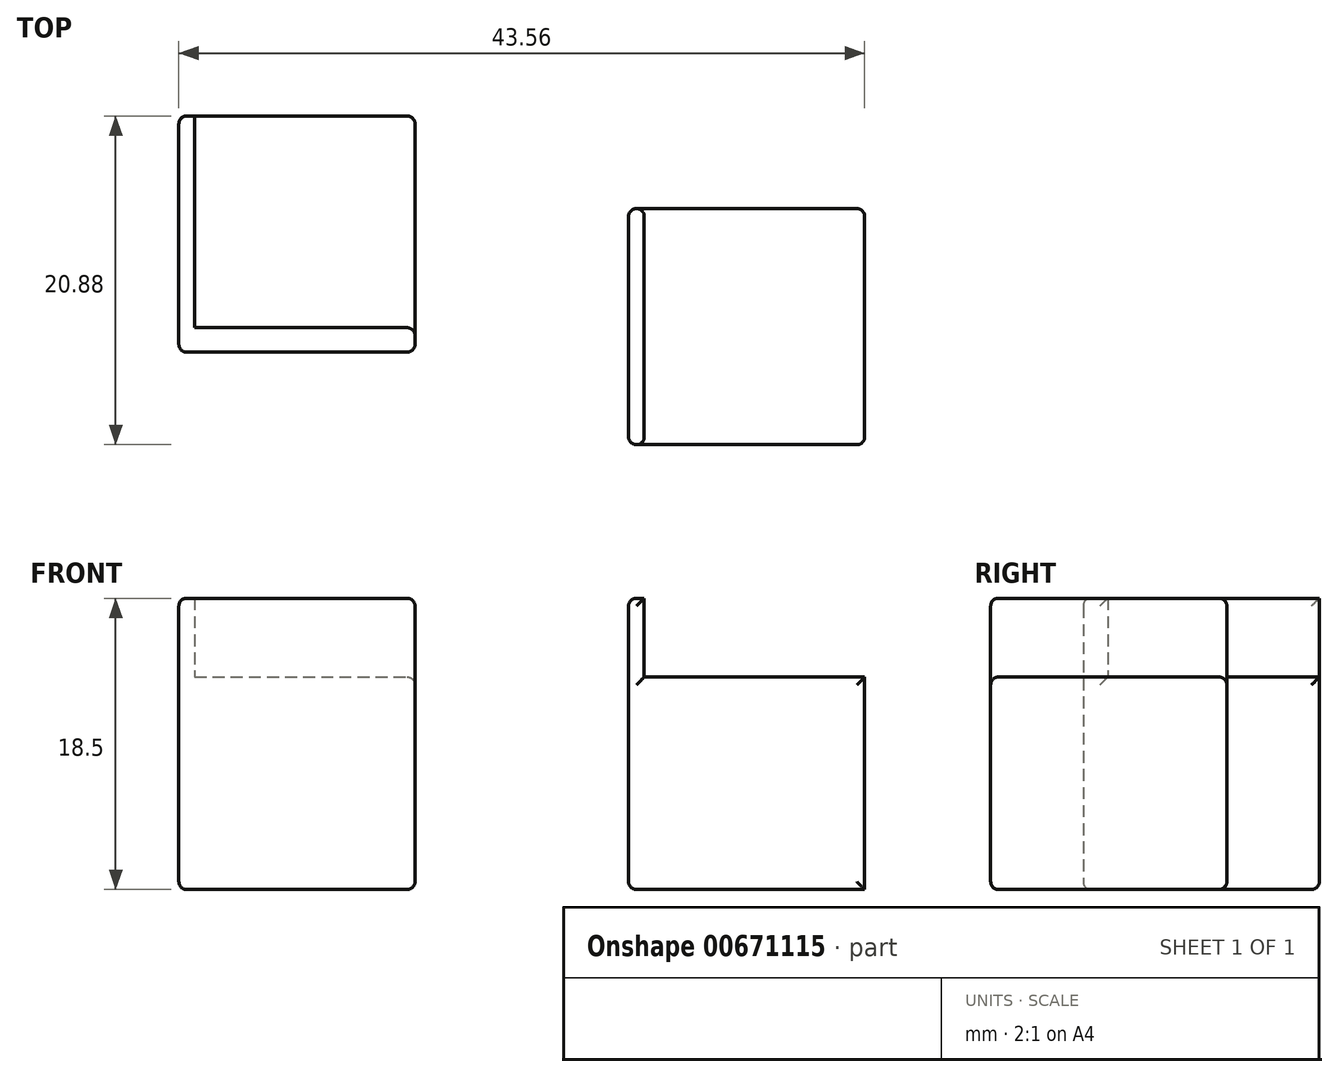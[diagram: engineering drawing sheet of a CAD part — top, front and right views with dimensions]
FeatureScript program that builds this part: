
annotation { "Feature Type Name" : "Feature", "Feature Type Description" : "" }
export const myFeature = defineFeature(function(context is Context, id is Id, definition is map)
    precondition{}
    {
        {
            var Q0;
            Q0=qCreatedBy(makeId("Top.planeOp"),FACE);
            var sketch = newSketch(context, id + "F0", { "sketchPlane" : qUnion([Q0])});
            skLineSegment(sketch, "E0.bottom", {"start": v(-22.19, -22.69) * mm, "end": v(-7.19, -22.69) * mm});
            skLineSegment(sketch, "E0.top", {"start": v(-22.19, -37.69) * mm, "end": v(-7.19, -37.69) * mm});
            skLineSegment(sketch, "E0.left", {"start": v(-22.19, -22.69) * mm, "end": v(-22.19, -37.69) * mm});
            skLineSegment(sketch, "E0.right", {"start": v(-7.19, -22.69) * mm, "end": v(-7.19, -37.69) * mm});
            skSolve(sketch);
        }
        {
            var Q0;
            Q0=makeQuery(id+"F0.imprint","IMPRINT",FACE,{"disambiguationData":[TD([[makeQuery(id+"F0.imprint","IMPRINT",EDGE,{"derivedFrom":sQuery(id+"F0.wireOp",EDGE,"E0.bottom")}),-1.0]])]});
            extrude(context, id + "F1", {"entities" : qUnion([Q0]), "depth" : 13.5 * mm, "offsetDistance" : 25 * mm});
        }
        {
            var Q0;
            Q0=makeQuery(id+"F1.opExtrude","CAP_FACE",FACE,{"disambiguationData":[OSD([sQuery(id+"F0.wireOp",EDGE,"E0.bottom"),sQuery(id+"F0.wireOp",EDGE,"E0.top"),sQuery(id+"F0.wireOp",EDGE,"E0.left"),sQuery(id+"F0.wireOp",EDGE,"E0.right")])],"isStart":false});
            var sketch = newSketch(context, id + "F2", { "sketchPlane" : qUnion([Q0])});
            skLineSegment(sketch, "E1.bottom", {"start": v(-22.19, -22.69) * mm, "end": v(-21.19, -22.69) * mm});
            skLineSegment(sketch, "E1.top", {"start": v(-22.19, -37.69) * mm, "end": v(-21.19, -37.69) * mm});
            skLineSegment(sketch, "E1.left", {"start": v(-22.19, -22.69) * mm, "end": v(-22.19, -37.69) * mm});
            skLineSegment(sketch, "E1.right", {"start": v(-21.19, -22.69) * mm, "end": v(-21.19, -37.69) * mm});
            skLineSegment(sketch, "E2.bottom", {"start": v(-22.19, -37.69) * mm, "end": v(-7.19, -37.69) * mm});
            skLineSegment(sketch, "E2.top", {"start": v(-22.19, -36.13) * mm, "end": v(-7.19, -36.13) * mm});
            skLineSegment(sketch, "E2.left", {"start": v(-22.19, -37.69) * mm, "end": v(-22.19, -36.13) * mm});
            skLineSegment(sketch, "E2.right", {"start": v(-7.19, -37.69) * mm, "end": v(-7.19, -36.13) * mm});
            skSolve(sketch);
        }
        {
            var Q0;
            Q0 = qSketchRegion(id + "F2", true);
            extrude(context, id + "F3", {"entities" : qUnion([Q0]), "operationType" : NewBodyOperationType.ADD, "depth" : 5 * mm, "offsetDistance" : 25 * mm});
        }
        {
            var Q0;
            Q0 = qSketchRegion(id + "F2", true);
            extrude(context, id + "F4", {"entities" : qUnion([Q0]), "operationType" : NewBodyOperationType.ADD, "depth" : 5 * mm, "offsetDistance" : 25 * mm});
        }
        {
            var Q0;
            Q0=makeQuery(id+"F3.boolean.opBoolean","MERGE",FACE,{"derivedFrom":[makeQuery(id+"F1.opExtrude","SWEPT_FACE",FACE,{"disambiguationData":[OSD([sQuery(id+"F0.wireOp",EDGE,"E0.left")])]}),makeQuery(id+"F3.opExtrude","SWEPT_FACE",FACE,{"disambiguationData":[OSD([sQuery(id+"F2.wireOp",EDGE,"E1.left"),sQuery(id+"F2.wireOp",EDGE,"E2.left")])]})]});
            var Q1;
            Q1=makeQuery(id+"F3.boolean.opBoolean","MERGE",FACE,{"derivedFrom":[makeQuery(id+"F1.opExtrude","SWEPT_FACE",FACE,{"disambiguationData":[OSD([sQuery(id+"F0.wireOp",EDGE,"E0.top")])]}),makeQuery(id+"F3.opExtrude","SWEPT_FACE",FACE,{"disambiguationData":[OSD([sQuery(id+"F2.wireOp",EDGE,"E2.bottom")])]})]});
            var Q2;
            Q2=makeQuery(id+"F1.opExtrude","CAP_FACE",FACE,{"disambiguationData":[OSD([sQuery(id+"F0.wireOp",EDGE,"E0.bottom"),sQuery(id+"F0.wireOp",EDGE,"E0.top"),sQuery(id+"F0.wireOp",EDGE,"E0.left"),sQuery(id+"F0.wireOp",EDGE,"E0.right")])],"isStart":true});
            var Q3;
            Q3=makeQuery(id+"F3.boolean.opBoolean","MERGE",FACE,{"derivedFrom":[makeQuery(id+"F1.opExtrude","SWEPT_FACE",FACE,{"disambiguationData":[OSD([sQuery(id+"F0.wireOp",EDGE,"E0.right")])]}),makeQuery(id+"F3.opExtrude","SWEPT_FACE",FACE,{"disambiguationData":[OSD([sQuery(id+"F2.wireOp",EDGE,"E2.right")])]})]});
            fillet(context, id + "F5", {"entities" : qUnion([Q0, Q1, Q2, Q3]), "radius" : 0.5 * mm, "tangentPropagation" : true, "allowEdgeOverflow" : false});
        }
        {
            var Q0;
            Q0=qCreatedBy(makeId("Top.planeOp"),FACE);
            var sketch = newSketch(context, id + "F6", { "sketchPlane" : qUnion([Q0])});
            skLineSegment(sketch, "E3.bottom", {"start": v(6.37, -28.57) * mm, "end": v(21.37, -28.57) * mm});
            skLineSegment(sketch, "E3.top", {"start": v(6.37, -43.57) * mm, "end": v(21.37, -43.57) * mm});
            skLineSegment(sketch, "E3.left", {"start": v(6.37, -28.57) * mm, "end": v(6.37, -43.57) * mm});
            skLineSegment(sketch, "E3.right", {"start": v(21.37, -28.57) * mm, "end": v(21.37, -43.57) * mm});
            skSolve(sketch);
        }
        {
            var Q0;
            Q0 = qSketchRegion(id + "F6", true);
            extrude(context, id + "F7", {"entities" : qUnion([Q0]), "depth" : 13.5 * mm, "offsetDistance" : 25 * mm});
        }
        {
            var Q0;
            Q0=makeQuery(id+"F7.opExtrude","CAP_FACE",FACE,{"disambiguationData":[OSD([sQuery(id+"F6.wireOp",EDGE,"E3.bottom"),sQuery(id+"F6.wireOp",EDGE,"E3.top"),sQuery(id+"F6.wireOp",EDGE,"E3.left"),sQuery(id+"F6.wireOp",EDGE,"E3.right")])],"isStart":false});
            var sketch = newSketch(context, id + "F8", { "sketchPlane" : qUnion([Q0])});
            skLineSegment(sketch, "E4.bottom", {"start": v(6.37, -43.57) * mm, "end": v(7.37, -43.57) * mm});
            skLineSegment(sketch, "E4.top", {"start": v(6.37, -28.57) * mm, "end": v(7.37, -28.57) * mm});
            skLineSegment(sketch, "E4.left", {"start": v(6.37, -43.57) * mm, "end": v(6.37, -28.57) * mm});
            skLineSegment(sketch, "E4.right", {"start": v(7.37, -43.57) * mm, "end": v(7.37, -28.57) * mm});
            skSolve(sketch);
        }
        {
            var Q0;
            Q0 = qSketchRegion(id + "F8", true);
            extrude(context, id + "F9", {"entities" : qUnion([Q0]), "operationType" : NewBodyOperationType.ADD, "depth" : 5 * mm, "offsetDistance" : 25 * mm});
        }
        {
            var Q0;
            Q0=makeQuery(id+"F9.boolean.opBoolean","MERGE",FACE,{"derivedFrom":[makeQuery(id+"F7.opExtrude","SWEPT_FACE",FACE,{"disambiguationData":[OSD([sQuery(id+"F6.wireOp",EDGE,"E3.left")])]}),makeQuery(id+"F9.opExtrude","SWEPT_FACE",FACE,{"disambiguationData":[OSD([sQuery(id+"F8.wireOp",EDGE,"E4.left")])]})]});
            var Q1;
            Q1=makeQuery(id+"F9.boolean.opBoolean","MERGE",FACE,{"derivedFrom":[makeQuery(id+"F7.opExtrude","SWEPT_FACE",FACE,{"disambiguationData":[OSD([sQuery(id+"F6.wireOp",EDGE,"E3.top")])]}),makeQuery(id+"F9.opExtrude","SWEPT_FACE",FACE,{"disambiguationData":[OSD([sQuery(id+"F8.wireOp",EDGE,"E4.bottom")])]})]});
            var Q2;
            Q2=makeQuery(id+"F9.boolean.opBoolean","MERGE",FACE,{"derivedFrom":[makeQuery(id+"F7.opExtrude","SWEPT_FACE",FACE,{"disambiguationData":[OSD([sQuery(id+"F6.wireOp",EDGE,"E3.bottom")])]}),makeQuery(id+"F9.opExtrude","SWEPT_FACE",FACE,{"disambiguationData":[OSD([sQuery(id+"F8.wireOp",EDGE,"E4.top")])]})]});
            fillet(context, id + "F10", {"entities" : qUnion([Q0, Q1, Q2]), "radius" : 0.5 * mm, "tangentPropagation" : true, "allowEdgeOverflow" : false});
        }
    });
